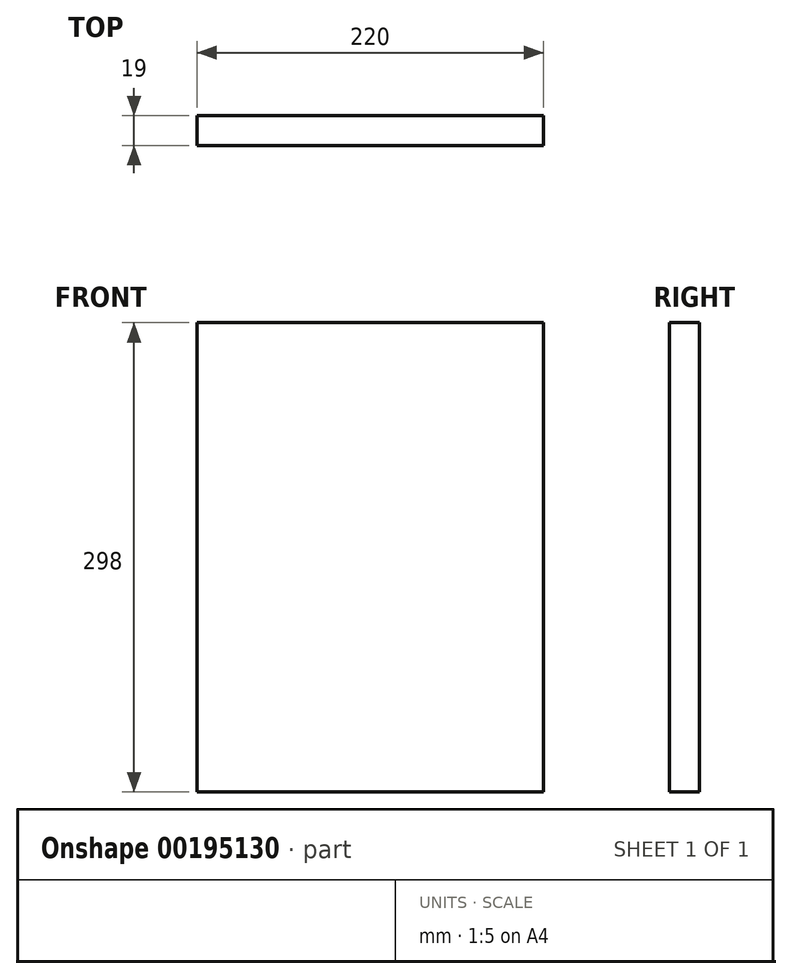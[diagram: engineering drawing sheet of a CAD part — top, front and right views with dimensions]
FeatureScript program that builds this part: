
annotation { "Feature Type Name" : "Feature", "Feature Type Description" : "" }
export const myFeature = defineFeature(function(context is Context, id is Id, definition is map)
    precondition{}
    {
        {
            var Q0;
            Q0=qCreatedBy(makeId("Front.planeOp"),FACE);
            var sketch = newSketch(context, id + "F0", { "sketchPlane" : qUnion([Q0])});
            skLineSegment(sketch, "E0.bottom", {"start": v(-19.97, 265.3) * mm, "end": v(200.03, 265.3) * mm});
            skLineSegment(sketch, "E0.top", {"start": v(-19.97, -32.7) * mm, "end": v(200.03, -32.7) * mm});
            skLineSegment(sketch, "E0.left", {"start": v(-19.97, 265.3) * mm, "end": v(-19.97, -32.7) * mm});
            skLineSegment(sketch, "E0.right", {"start": v(200.03, 265.3) * mm, "end": v(200.03, -32.7) * mm});
            skSolve(sketch);
        }
        {
            var Q0;
            Q0=makeQuery(id+"F0.imprint","IMPRINT",FACE,{"disambiguationData":[TD([[makeQuery(id+"F0.imprint","IMPRINT",EDGE,{"derivedFrom":sQuery(id+"F0.wireOp",EDGE,"E0.bottom")}),-1.0]])]});
            extrude(context, id + "F1", {"entities" : qUnion([Q0]), "depth" : 19 * mm});
        }
    });
